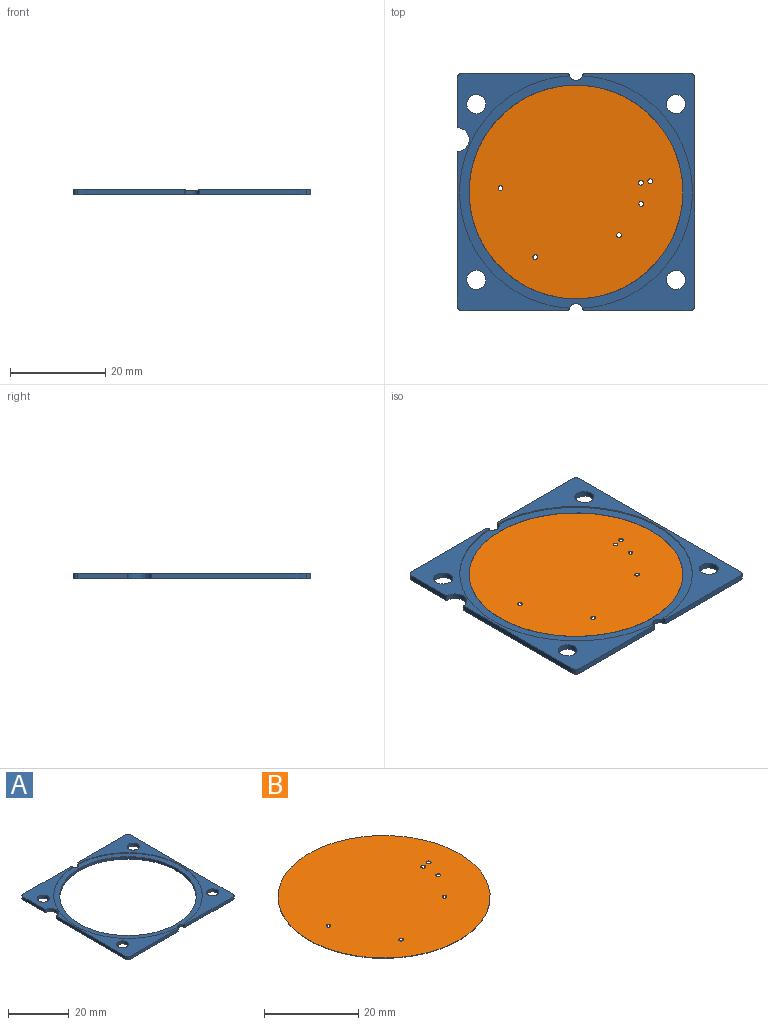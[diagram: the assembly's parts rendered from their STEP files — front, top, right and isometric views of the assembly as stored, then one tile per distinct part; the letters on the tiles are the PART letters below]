
ASSEMBLY  parts=2 mates=1
PART A: 25 faces, bbox 50x50x1.2 mm
  f0: cylinder r=1.5mm len=3mm, axis (0,0,-1), area 4.8mm2, adj f2,f5,f6,f19,f20,f21,f22,f23
  f1: cylinder r=1.5mm len=3mm, axis (0,0,-1), area 4.8mm2, adj f2,f12,f13,f19,f20,f21,f22,f23
  f2: plane 50x23.6mm, normal (0,0,1), area 279.9mm2, adj f0,f1,f3,f4,f5,f13,f15,f16
  f3: plane 48x1.2mm, normal (1,0,0), area 57.6mm2, adj f2,f4,f18,f20
  f4: cylinder r=1mm len=1.2mm, axis (0,0,-1), area 1.9mm2, adj f2,f3,f5,f20
  f5: plane 22.5x1.2mm, normal (0,1,0), area 27mm2, adj f0,f2,f4,f20
  f6: plane 22.5x1.2mm, normal (0,1,0), area 27mm2, adj f0,f7,f19,f20
  f7: cylinder r=1mm len=1.2mm, axis (0,0,-1), area 1.9mm2, adj f6,f8,f19,f20
  f8: plane 10.5x1.2mm, normal (-1,0,0), area 12.6mm2, adj f7,f9,f19,f20
  f9: cylinder r=2.5mm len=5mm, axis (0,0,-1), area 9.4mm2, adj f8,f10,f19,f20
  f10: plane 32.5x1.2mm, normal (-1,0,0), area 39mm2, adj f9,f11,f19,f20
  f11: cylinder r=1mm len=1.2mm, axis (0,0,-1), area 1.9mm2, adj f10,f12,f19,f20
  f12: plane 22.5x1.2mm, normal (0,-1,0), area 27mm2, adj f1,f11,f19,f20
  f13: plane 22.5x1.2mm, normal (0,-1,0), area 27mm2, adj f1,f2,f18,f20
  f14: cylinder r=2mm len=4.01mm, axis (0,0,-1), area 15.1mm2, adj f19,f20
  f15: cylinder r=2mm len=4.01mm, axis (0,0,-1), area 15.1mm2, adj f2,f20
  f16: cylinder r=2mm len=4.01mm, axis (0,0,-1), area 15.1mm2, adj f2,f20
  f17: cylinder r=2mm len=4.01mm, axis (0,0,-1), area 15.1mm2, adj f19,f20
  f18: cylinder r=1mm len=1.2mm, axis (0,0,-1), area 1.9mm2, adj f2,f3,f13,f20
  f19: plane 50x23.6mm, normal (0,0,1), area 270.1mm2, adj f0,f1,f6,f7,f8,f9,f10,f11
  f20: plane 50x50mm, normal (0,0,-1), area 841.3mm2, adj f0,f1,f3,f4,f5,f6,f7,f8
  f21: cylinder r=24.5mm len=48.92mm, axis (0,0,1), area 18.2mm2, adj f0,f1,f2,f23
  f22: cylinder r=24.5mm len=48.92mm, axis (0,0,1), area 18.2mm2, adj f0,f1,f19,f23
  f23: plane 49x48.92mm, normal (0,0,1), area 291.3mm2, adj f0,f1,f21,f22,f24
  f24: cylinder r=22.5mm len=45mm, axis (0,0,-1), area 135mm2, adj f20,f23
PART B: 9 faces, bbox 45x45x0.1 mm
  f0: cylinder r=22.5mm len=45mm, axis (0,0,-1), area 14.1mm2, adj f1,f2
  f1: plane 45x45mm, normal (0,0,1), area 1585.7mm2, adj f0,f3,f4,f5,f6,f7,f8
  f2: plane 45x45mm, normal (0,0,-1), area 1585.7mm2, adj f0,f3,f4,f5,f6,f7,f8
  f3: cylinder r=0.5mm len=1mm, axis (0,0,1), area 0.3mm2, adj f1,f2
  f4: cylinder r=0.5mm len=1mm, axis (0,0,1), area 0.3mm2, adj f1,f2
  f5: cylinder r=0.5mm len=1mm, axis (0,0,1), area 0.3mm2, adj f1,f2
  f6: cylinder r=0.5mm len=1mm, axis (0,0,1), area 0.3mm2, adj f1,f2
  f7: cylinder r=0.5mm len=1mm, axis (0,0,1), area 0.3mm2, adj f1,f2
  f8: cylinder r=0.5mm len=1mm, axis (0,0,1), area 0.3mm2, adj f1,f2
PLACE A at identity
PLACE B t=(0,0,0.85)mm
MATE fastened A.f24 <-> B.f0  axis (0,0,1) through (0,0,0.95)mm
